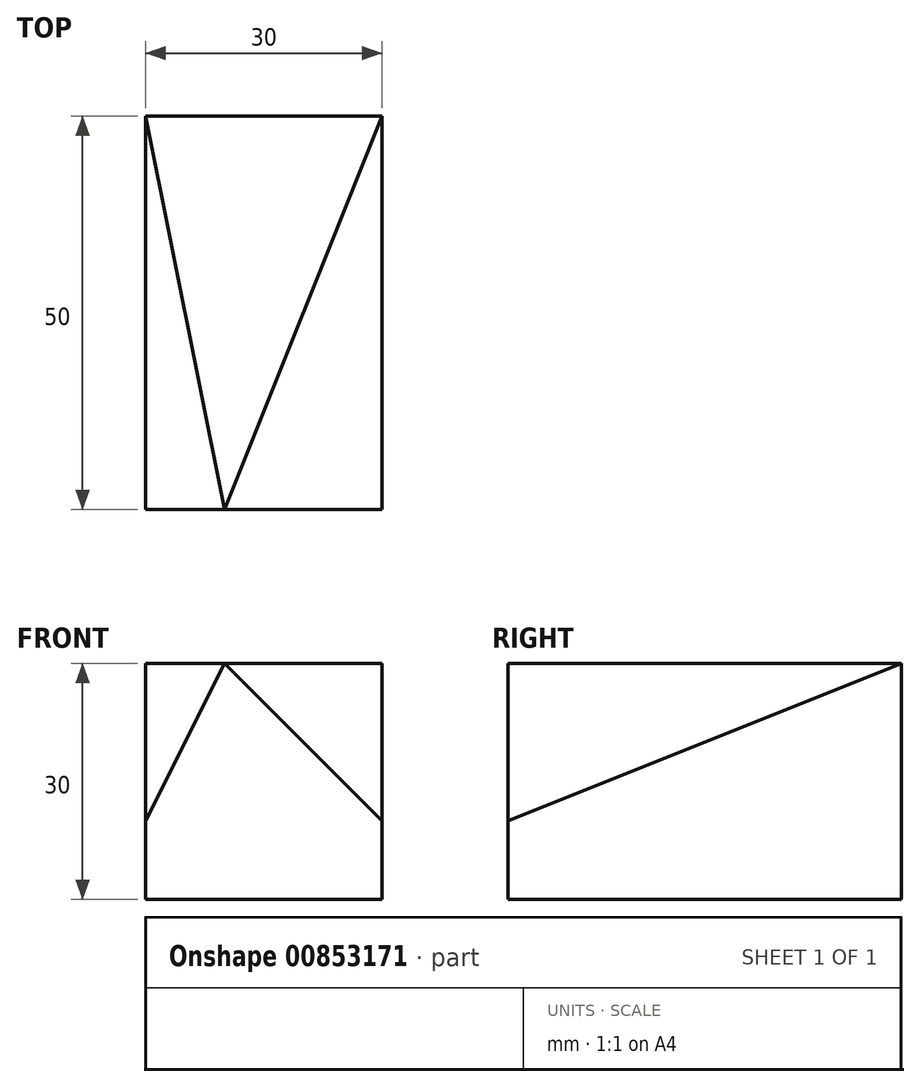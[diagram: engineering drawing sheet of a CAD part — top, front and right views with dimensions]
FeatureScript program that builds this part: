
annotation { "Feature Type Name" : "Feature", "Feature Type Description" : "" }
export const myFeature = defineFeature(function(context is Context, id is Id, definition is map)
    precondition{}
    {
        {
            var Q0;
            Q0=qCreatedBy(makeId("Top.planeOp"),FACE);
            var sketch = newSketch(context, id + "F0", { "sketchPlane" : qUnion([Q0])});
            skLineSegment(sketch, "E0.bottom", {"start": v(-15, -25) * mm, "end": v(15, -25) * mm});
            skLineSegment(sketch, "E0.top", {"start": v(-15, 25) * mm, "end": v(15, 25) * mm});
            skLineSegment(sketch, "E0.left", {"start": v(-15, -25) * mm, "end": v(-15, 25) * mm});
            skLineSegment(sketch, "E0.right", {"start": v(15, -25) * mm, "end": v(15, 25) * mm});
            skSolve(sketch);
        }
        {
            var Q0;
            Q0=makeQuery(id+"F0.imprint","IMPRINT",FACE,{"disambiguationData":[TD([[makeQuery(id+"F0.imprint","IMPRINT",EDGE,{"derivedFrom":sQuery(id+"F0.wireOp",EDGE,"E0.bottom")}),1.0]])]});
            extrude(context, id + "F1", {"entities" : qUnion([Q0]), "depth" : 30 * mm, "offsetDistance" : 25 * mm});
        }
        {
            var Q0;
            Q0=makeQuery(id+"F1.opExtrude","SWEPT_FACE",FACE,{"disambiguationData":[OSD([sQuery(id+"F0.wireOp",EDGE,"E0.bottom")])]});
            var sketch = newSketch(context, id + "F2", { "sketchPlane" : qUnion([Q0])});
            skLineSegment(sketch, "E1", {"start": v(-15, 10) * mm, "end": v(-15, 30) * mm});
            skLineSegment(sketch, "E2", {"start": v(-15, 30) * mm, "end": v(-5, 30) * mm});
            skLineSegment(sketch, "E3", {"start": v(-5, 30) * mm, "end": v(-15, 10) * mm});
            skLineSegment(sketch, "E4", {"start": v(-5, 30) * mm, "end": v(15, 30) * mm});
            skLineSegment(sketch, "E5", {"start": v(15, 30) * mm, "end": v(15, 10) * mm});
            skLineSegment(sketch, "E6", {"start": v(15, 10) * mm, "end": v(-5, 30) * mm});
            skSolve(sketch);
        }
        {
            var Q0;
            Q0=makeQuery(id+"F1.opExtrude","SWEPT_FACE",FACE,{"disambiguationData":[OSD([sQuery(id+"F0.wireOp",EDGE,"E0.right")])]});
            var sketch = newSketch(context, id + "F3", { "sketchPlane" : qUnion([Q0])});
            skLineSegment(sketch, "E7", {"start": v(25, 30) * mm, "end": v(-25, 10) * mm});
            skSolve(sketch);
        }
        {
            var Q0;
            Q0 = qSketchRegion(id + "F2", true);
            var Q1;
            Q1=sQuery(id+"F3.wireOp",EDGE,"E7");
            sweep(context, id + "F4", {"operationType" : NewBodyOperationType.REMOVE, "profiles" : qUnion([Q0]), "path" : qUnion([Q1])});
        }
    });
